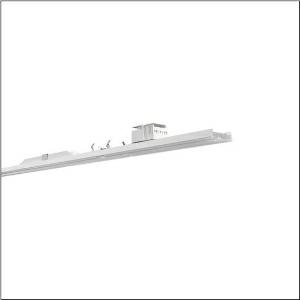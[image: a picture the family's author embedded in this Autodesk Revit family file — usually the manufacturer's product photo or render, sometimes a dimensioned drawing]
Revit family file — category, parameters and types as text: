
# Revit family: licross_r__11_recessed_mo_51tl19dn49xf_048a
name_source: partatom
category: Lighting Fixtures
units: mm (PartAtom-declared; Revit-internal decimal feet)

## family parameters
Cut with Voids When Loaded = No
Host = Face
Light Source = No
Part Type = Normal
Room Calculation Point = No
Round Connector Dimension = Use Diameter
Shared = No

## types (1)
- --- (1 x LED, 9010 lm, 56.9 W, 4000K)
    Apparent Load = 57 VA
    CIE Flux Codes = 55 90 98 100 100
    Color Rendering = 80
    Color Temperature = 4000K
    Default Elevation = 1800 mm
    Description = Licross® 11 Recessed MOluminaire insert, length: 1.500mm, width: 66mm, height: 67mm, LED rated luminous flux: 9.010lm, light colour: 840, control gear: DALI 2, control gear: ECG DALI, with plug, 5-pole, with phase selection, mains connection: 220..240V, AC, 50/60Hz, halogen-free wiring, primary light control with lens, of plastic, primary optical cover: cover, of PMMA, light emission: direct distribution, primary light characteristic: double asymmetric, protection rating (complete): IP40, insulation class (complete): insulation class I (protective earthing), certification: CE, ENEC, VDE, protection symbol: D if used in an environment without relevant dust loads with corresponding accessories, permissible ambient temperature for indoor applications: -25..+35°C, reducing of maximum allowable ambient temperature of 5°C with ceiling mounting, corresponds to IFS (International Featured Standards) requirements for safety and quality in the food industry, packaging unit: 1 piece
    Height = 58 mm
    Lamp = 1 x LED
    Lamp Light Flux = 9010 lm
    Lamp Power = 56.9 W
    Lamp count = 1
    Length = 1500 mm
    Luminous efficacy = 158 lm/W
    Manufacturer = Siteco
    ModVariant = No
    Model = 51TL19DN49XF
    Mounting Place = Ceiling
    Mounting Type = Pendant
    Number of Poles = 1
    OnlyDefault = Yes
    Power Factor = 1
    Product Name = Licross® 11 Recessed MO
    Product group = luminaire insert
    ProductGroupID = 902
    Protection Class = Protection class I
    Protection Degree = IP 40
    RLX_Detail_Level = 1
    RlxData = <blob elided: 22253 chars, md5=21a5df34>
    Socket = socket
    Standby Power = 0 W
    System Light Flux = 9010 lm
    System Power = 57 W
    Type Comments = factory setting: luminous flux: 100 % | dim-lin: 254 | 375 mA
    Type Image = l_1266722.jpg
    URL = http://relux.com
    VarID = @adj_138919
    Voltage = 0 V
    Weight = 0.00 kg
    Width = 66 mm

## geometry (parser evidence)
native form markers: Blend x4, Sweep x11
no freeform markers — native parametric forms only
